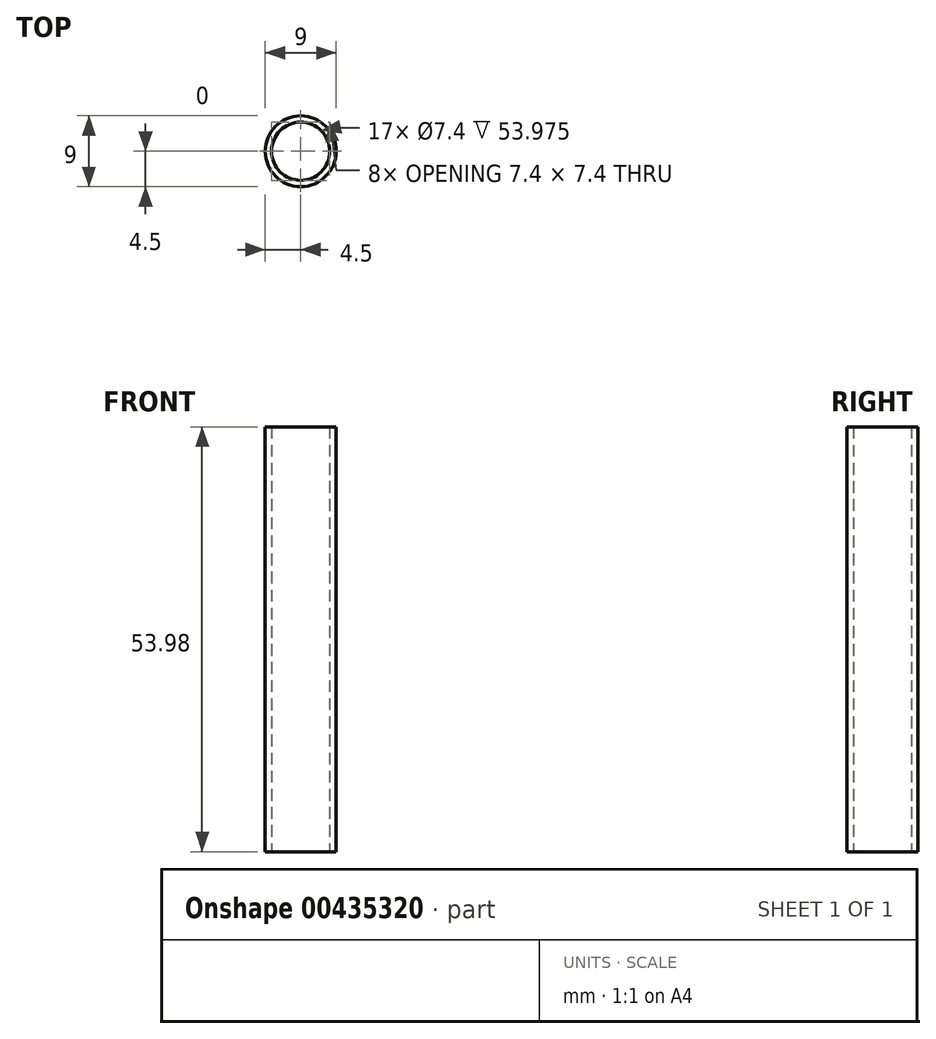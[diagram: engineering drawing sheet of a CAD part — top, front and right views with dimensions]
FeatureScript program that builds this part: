
annotation { "Feature Type Name" : "Feature", "Feature Type Description" : "" }
export const myFeature = defineFeature(function(context is Context, id is Id, definition is map)
    precondition{}
    {
        {
            var Q0;
            Q0=qCreatedBy(makeId("Top.planeOp"),FACE);
            var sketch = newSketch(context, id + "F0", { "sketchPlane" : qUnion([Q0])});
            skCircle(sketch, "E0", {"center": v(0, 0) * mm, "radius": 4.5 * mm});
            skSolve(sketch);
        }
        {
            var Q0;
            Q0=makeQuery(id+"F0.imprint","IMPRINT",FACE,{"disambiguationData":[TD([[makeQuery(id+"F0.imprint","IMPRINT",EDGE,{"derivedFrom":sQuery(id+"F0.wireOp",EDGE,"E0")}),1.0]])]});
            extrude(context, id + "F1", {"entities" : qUnion([Q0]), "depth" : 53.98 * mm});
        }
        {
            var Q0;
            Q0=qCreatedBy(makeId("Top.planeOp"),FACE);
            var sketch = newSketch(context, id + "F2", { "sketchPlane" : qUnion([Q0])});
            skCircle(sketch, "E1", {"center": v(0, 0) * mm, "radius": 3.7 * mm});
            skSolve(sketch);
        }
        {
            var Q0;
            Q0=sQuery(id+"F2.wireOp",VERTEX,"E1.center");
            var Q1;
            Q1=makeQuery(id+"F1.opExtrude","SWEPT_BODY",BODY,{"disambiguationData":[OSD([sQuery(id+"F0.wireOp",EDGE,"E0")])]});
            hole(context, id + "F3", {"style" : HoleStyle.SIMPLE, "endStyle" : HoleEndStyle.THROUGH, "oppositeDirection" : true, "holeDiameter" : 7.4 * mm, "isTappedThrough" : true, "tappedDepth" : 12 * mm, "tapClearance" : 3, "locations" : qUnion([Q0]), "scope" : qUnion([Q1])});
        }
    });
